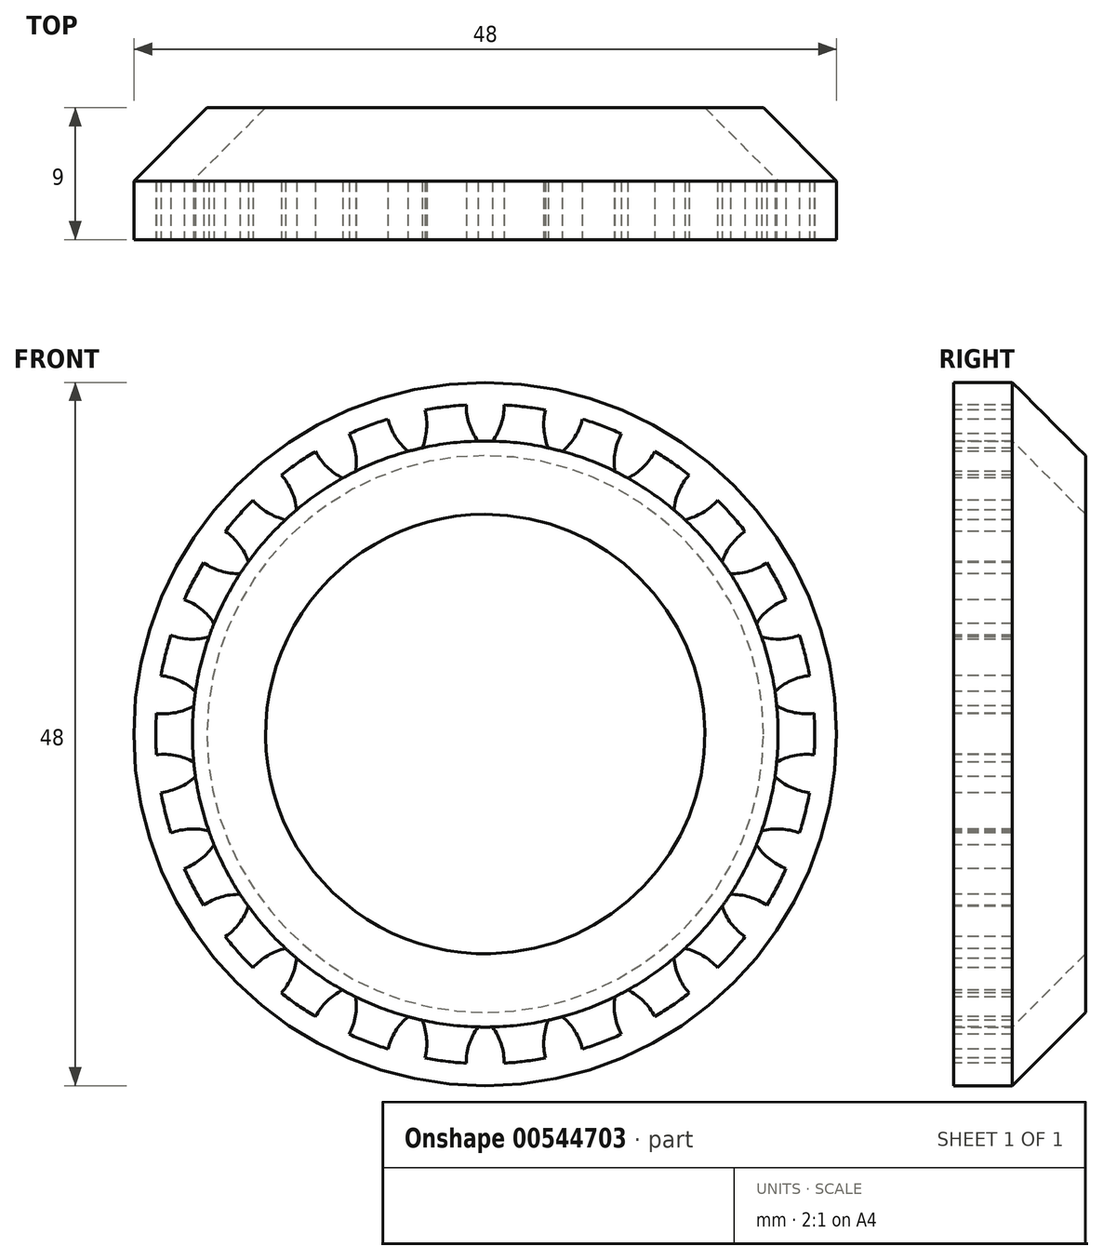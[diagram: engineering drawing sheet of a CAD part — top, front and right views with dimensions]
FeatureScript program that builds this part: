
annotation { "Feature Type Name" : "Feature", "Feature Type Description" : "" }
export const myFeature = defineFeature(function(context is Context, id is Id, definition is map)
    precondition{}
    {
        {
            var Q0;
            Q0=qCreatedBy(makeId("Right.planeOp"),FACE);
            var sketch = newSketch(context, id + "F0", { "sketchPlane" : qUnion([Q0])});
            skLineSegment(sketch, "E0", {"start": v(0, 0) * mm, "end": v(-8.99, 0) * mm, "construction": true});
            skLineSegment(sketch, "E1", {"start": v(0, 20) * mm, "end": v(4, 20) * mm});
            skLineSegment(sketch, "E2", {"start": v(4, 20) * mm, "end": v(9, 15) * mm});
            skLineSegment(sketch, "E3", {"start": v(9, 15) * mm, "end": v(9, 19) * mm});
            skLineSegment(sketch, "E4", {"start": v(9, 19) * mm, "end": v(4, 24) * mm});
            skLineSegment(sketch, "E5", {"start": v(4, 24) * mm, "end": v(0, 24) * mm});
            skLineSegment(sketch, "E6", {"start": v(0, 24) * mm, "end": v(0, 20) * mm});
            skSolve(sketch);
        }
        {
            var Q0;
            Q0 = qSketchRegion(id + "F0", true);
            var Q1;
            Q1=sQuery(id+"F0.wireOp",EDGE,"E0");
            revolve(context, id + "F1", {"entities" : qUnion([Q0]), "axis" : qUnion([Q1]), "revolveType" : RevolveType.FULL});
        }
        {
            var Q0;
            Q0=qCreatedBy(makeId("Front.planeOp"),FACE);
            var sketch = newSketch(context, id + "F2", { "sketchPlane" : qUnion([Q0])});
            skCircle(sketch, "E7", {"center": v(0, 0) * mm, "radius": 20 * mm});
            skCircle(sketch, "E8", {"center": v(0, 0) * mm, "radius": 24 * mm, "construction": true});
            skCircle(sketch, "E9", {"center": v(0, 0) * mm, "radius": 22.5 * mm});
            skPoint(sketch, "E10", {"position": v(0, 20) * mm});
            skPoint(sketch, "E11", {"position": v(-0.5, 20) * mm});
            skPoint(sketch, "E12", {"position": v(0.5, 20) * mm});
            skPoint(sketch, "E13", {"position": v(0, 22.5) * mm});
            skPoint(sketch, "E14", {"position": v(-1.3, 22.46) * mm});
            skPoint(sketch, "E15", {"position": v(1.3, 22.46) * mm});
            skArc(sketch, "E16", {"start": v(-1.3, 22.46) * mm, "mid": v(-1.1, 21.17) * mm, "end": v(-0.5, 20) * mm});
            skArc(sketch, "E17", {"start": v(0.5, 20) * mm, "mid": v(1.1, 21.17) * mm, "end": v(1.3, 22.46) * mm});
            skLineSegment(sketch, "E18", {"start": v(-0.5, 20) * mm, "end": v(0.5, 20) * mm});
            skPoint(sketch, "E19.1.0", {"position": v(-5.27, 19.3) * mm});
            skArc(sketch, "E19.1.1", {"start": v(-4.3, 19.53) * mm, "mid": v(-4, 20.81) * mm, "end": v(-4.11, 22.12) * mm});
            skArc(sketch, "E19.1.2", {"start": v(-6.64, 21.5) * mm, "mid": v(-6.13, 20.29) * mm, "end": v(-5.27, 19.3) * mm});
            skPoint(sketch, "E19.1.3", {"position": v(-6.64, 21.5) * mm});
            skPoint(sketch, "E19.1.4", {"position": v(-5.38, 21.85) * mm});
            skPoint(sketch, "E19.1.5", {"position": v(-4.3, 19.53) * mm});
            skPoint(sketch, "E19.1.6", {"position": v(-4.11, 22.12) * mm});
            skPoint(sketch, "E19.1.7", {"position": v(-4.79, 19.42) * mm});
            skLineSegment(sketch, "E19.1.8", {"start": v(-5.27, 19.3) * mm, "end": v(-4.3, 19.53) * mm});
            skPoint(sketch, "E19.2.0", {"position": v(-9.73, 17.47) * mm});
            skArc(sketch, "E19.2.1", {"start": v(-8.85, 17.94) * mm, "mid": v(-8.87, 19.25) * mm, "end": v(-9.29, 20.5) * mm});
            skArc(sketch, "E19.2.2", {"start": v(-11.59, 19.29) * mm, "mid": v(-10.8, 18.23) * mm, "end": v(-9.73, 17.47) * mm});
            skPoint(sketch, "E19.2.3", {"position": v(-11.59, 19.29) * mm});
            skPoint(sketch, "E19.2.4", {"position": v(-10.46, 19.92) * mm});
            skPoint(sketch, "E19.2.5", {"position": v(-8.85, 17.94) * mm});
            skPoint(sketch, "E19.2.6", {"position": v(-9.29, 20.5) * mm});
            skPoint(sketch, "E19.2.7", {"position": v(-9.3, 17.7) * mm});
            skLineSegment(sketch, "E19.2.8", {"start": v(-9.73, 17.47) * mm, "end": v(-8.85, 17.94) * mm});
            skPoint(sketch, "E19.3.0", {"position": v(-13.63, 14.63) * mm});
            skArc(sketch, "E19.3.1", {"start": v(-12.88, 15.3) * mm, "mid": v(-13.22, 16.57) * mm, "end": v(-13.92, 17.67) * mm});
            skArc(sketch, "E19.3.2", {"start": v(-15.87, 15.95) * mm, "mid": v(-14.85, 15.12) * mm, "end": v(-13.63, 14.63) * mm});
            skPoint(sketch, "E19.3.3", {"position": v(-15.87, 15.95) * mm});
            skPoint(sketch, "E19.3.4", {"position": v(-14.92, 16.84) * mm});
            skPoint(sketch, "E19.3.5", {"position": v(-12.88, 15.3) * mm});
            skPoint(sketch, "E19.3.6", {"position": v(-13.92, 17.67) * mm});
            skPoint(sketch, "E19.3.7", {"position": v(-13.26, 14.97) * mm});
            skLineSegment(sketch, "E19.3.8", {"start": v(-13.63, 14.63) * mm, "end": v(-12.88, 15.3) * mm});
            skPoint(sketch, "E19.4.0", {"position": v(-16.74, 10.95) * mm});
            skArc(sketch, "E19.4.1", {"start": v(-16.17, 11.77) * mm, "mid": v(-16.8, 12.92) * mm, "end": v(-17.75, 13.83) * mm});
            skArc(sketch, "E19.4.2", {"start": v(-19.22, 11.7) * mm, "mid": v(-18.04, 11.12) * mm, "end": v(-16.74, 10.95) * mm});
            skPoint(sketch, "E19.4.3", {"position": v(-19.22, 11.7) * mm});
            skPoint(sketch, "E19.4.4", {"position": v(-18.52, 12.78) * mm});
            skPoint(sketch, "E19.4.5", {"position": v(-16.17, 11.77) * mm});
            skPoint(sketch, "E19.4.6", {"position": v(-17.75, 13.83) * mm});
            skPoint(sketch, "E19.4.7", {"position": v(-16.46, 11.36) * mm});
            skLineSegment(sketch, "E19.4.8", {"start": v(-16.74, 10.95) * mm, "end": v(-16.17, 11.77) * mm});
            skPoint(sketch, "E19.5.0", {"position": v(-18.87, 6.62) * mm});
            skArc(sketch, "E19.5.1", {"start": v(-18.52, 7.56) * mm, "mid": v(-19.4, 8.53) * mm, "end": v(-20.54, 9.18) * mm});
            skArc(sketch, "E19.5.2", {"start": v(-21.46, 6.75) * mm, "mid": v(-20.18, 6.48) * mm, "end": v(-18.87, 6.62) * mm});
            skPoint(sketch, "E19.5.3", {"position": v(-21.46, 6.75) * mm});
            skPoint(sketch, "E19.5.4", {"position": v(-21.04, 7.98) * mm});
            skPoint(sketch, "E19.5.5", {"position": v(-18.52, 7.56) * mm});
            skPoint(sketch, "E19.5.6", {"position": v(-20.54, 9.18) * mm});
            skPoint(sketch, "E19.5.7", {"position": v(-18.7, 7.1) * mm});
            skLineSegment(sketch, "E19.5.8", {"start": v(-18.87, 6.62) * mm, "end": v(-18.52, 7.56) * mm});
            skPoint(sketch, "E19.6.0", {"position": v(-19.9, 1.91) * mm});
            skArc(sketch, "E19.6.1", {"start": v(-19.79, 2.9) * mm, "mid": v(-20.88, 3.64) * mm, "end": v(-22.14, 4) * mm});
            skArc(sketch, "E19.6.2", {"start": v(-22.46, 1.42) * mm, "mid": v(-21.14, 1.46) * mm, "end": v(-19.9, 1.91) * mm});
            skPoint(sketch, "E19.6.3", {"position": v(-22.46, 1.42) * mm});
            skPoint(sketch, "E19.6.4", {"position": v(-22.34, 2.71) * mm});
            skPoint(sketch, "E19.6.5", {"position": v(-19.79, 2.9) * mm});
            skPoint(sketch, "E19.6.6", {"position": v(-22.14, 4) * mm});
            skPoint(sketch, "E19.6.7", {"position": v(-19.85, 2.41) * mm});
            skLineSegment(sketch, "E19.6.8", {"start": v(-19.9, 1.91) * mm, "end": v(-19.79, 2.9) * mm});
            skPoint(sketch, "E19.7.0", {"position": v(-19.79, -2.9) * mm});
            skArc(sketch, "E19.7.1", {"start": v(-19.9, -1.91) * mm, "mid": v(-21.14, -1.46) * mm, "end": v(-22.46, -1.42) * mm});
            skArc(sketch, "E19.7.2", {"start": v(-22.14, -4) * mm, "mid": v(-20.88, -3.64) * mm, "end": v(-19.79, -2.9) * mm});
            skPoint(sketch, "E19.7.3", {"position": v(-22.14, -4) * mm});
            skPoint(sketch, "E19.7.4", {"position": v(-22.34, -2.71) * mm});
            skPoint(sketch, "E19.7.5", {"position": v(-19.9, -1.91) * mm});
            skPoint(sketch, "E19.7.6", {"position": v(-22.46, -1.42) * mm});
            skPoint(sketch, "E19.7.7", {"position": v(-19.85, -2.41) * mm});
            skLineSegment(sketch, "E19.7.8", {"start": v(-19.79, -2.9) * mm, "end": v(-19.9, -1.91) * mm});
            skPoint(sketch, "E19.8.0", {"position": v(-18.52, -7.56) * mm});
            skArc(sketch, "E19.8.1", {"start": v(-18.87, -6.62) * mm, "mid": v(-20.18, -6.48) * mm, "end": v(-21.46, -6.75) * mm});
            skArc(sketch, "E19.8.2", {"start": v(-20.54, -9.18) * mm, "mid": v(-19.4, -8.53) * mm, "end": v(-18.52, -7.56) * mm});
            skPoint(sketch, "E19.8.3", {"position": v(-20.54, -9.18) * mm});
            skPoint(sketch, "E19.8.4", {"position": v(-21.04, -7.98) * mm});
            skPoint(sketch, "E19.8.5", {"position": v(-18.87, -6.62) * mm});
            skPoint(sketch, "E19.8.6", {"position": v(-21.46, -6.75) * mm});
            skPoint(sketch, "E19.8.7", {"position": v(-18.7, -7.1) * mm});
            skLineSegment(sketch, "E19.8.8", {"start": v(-18.52, -7.56) * mm, "end": v(-18.87, -6.62) * mm});
            skPoint(sketch, "E19.9.0", {"position": v(-16.17, -11.77) * mm});
            skArc(sketch, "E19.9.1", {"start": v(-16.74, -10.95) * mm, "mid": v(-18.04, -11.12) * mm, "end": v(-19.22, -11.7) * mm});
            skArc(sketch, "E19.9.2", {"start": v(-17.75, -13.83) * mm, "mid": v(-16.8, -12.92) * mm, "end": v(-16.17, -11.77) * mm});
            skPoint(sketch, "E19.9.3", {"position": v(-17.75, -13.83) * mm});
            skPoint(sketch, "E19.9.4", {"position": v(-18.52, -12.78) * mm});
            skPoint(sketch, "E19.9.5", {"position": v(-16.74, -10.95) * mm});
            skPoint(sketch, "E19.9.6", {"position": v(-19.22, -11.7) * mm});
            skPoint(sketch, "E19.9.7", {"position": v(-16.46, -11.36) * mm});
            skLineSegment(sketch, "E19.9.8", {"start": v(-16.17, -11.77) * mm, "end": v(-16.74, -10.95) * mm});
            skPoint(sketch, "E19.10.0", {"position": v(-12.88, -15.3) * mm});
            skArc(sketch, "E19.10.1", {"start": v(-13.63, -14.63) * mm, "mid": v(-14.85, -15.12) * mm, "end": v(-15.87, -15.95) * mm});
            skArc(sketch, "E19.10.2", {"start": v(-13.92, -17.67) * mm, "mid": v(-13.22, -16.57) * mm, "end": v(-12.88, -15.3) * mm});
            skPoint(sketch, "E19.10.3", {"position": v(-13.92, -17.67) * mm});
            skPoint(sketch, "E19.10.4", {"position": v(-14.92, -16.84) * mm});
            skPoint(sketch, "E19.10.5", {"position": v(-13.63, -14.63) * mm});
            skPoint(sketch, "E19.10.6", {"position": v(-15.87, -15.95) * mm});
            skPoint(sketch, "E19.10.7", {"position": v(-13.26, -14.97) * mm});
            skLineSegment(sketch, "E19.10.8", {"start": v(-12.88, -15.3) * mm, "end": v(-13.63, -14.63) * mm});
            skPoint(sketch, "E19.11.0", {"position": v(-8.85, -17.94) * mm});
            skArc(sketch, "E19.11.1", {"start": v(-9.73, -17.47) * mm, "mid": v(-10.8, -18.23) * mm, "end": v(-11.59, -19.29) * mm});
            skArc(sketch, "E19.11.2", {"start": v(-9.29, -20.5) * mm, "mid": v(-8.87, -19.25) * mm, "end": v(-8.85, -17.94) * mm});
            skPoint(sketch, "E19.11.3", {"position": v(-9.29, -20.5) * mm});
            skPoint(sketch, "E19.11.4", {"position": v(-10.46, -19.92) * mm});
            skPoint(sketch, "E19.11.5", {"position": v(-9.73, -17.47) * mm});
            skPoint(sketch, "E19.11.6", {"position": v(-11.59, -19.29) * mm});
            skPoint(sketch, "E19.11.7", {"position": v(-9.3, -17.7) * mm});
            skLineSegment(sketch, "E19.11.8", {"start": v(-8.85, -17.94) * mm, "end": v(-9.73, -17.47) * mm});
            skPoint(sketch, "E19.12.0", {"position": v(-4.3, -19.53) * mm});
            skArc(sketch, "E19.12.1", {"start": v(-5.27, -19.3) * mm, "mid": v(-6.13, -20.29) * mm, "end": v(-6.64, -21.5) * mm});
            skArc(sketch, "E19.12.2", {"start": v(-4.11, -22.12) * mm, "mid": v(-4, -20.81) * mm, "end": v(-4.3, -19.53) * mm});
            skPoint(sketch, "E19.12.3", {"position": v(-4.11, -22.12) * mm});
            skPoint(sketch, "E19.12.4", {"position": v(-5.38, -21.85) * mm});
            skPoint(sketch, "E19.12.5", {"position": v(-5.27, -19.3) * mm});
            skPoint(sketch, "E19.12.6", {"position": v(-6.64, -21.5) * mm});
            skPoint(sketch, "E19.12.7", {"position": v(-4.79, -19.42) * mm});
            skLineSegment(sketch, "E19.12.8", {"start": v(-4.3, -19.53) * mm, "end": v(-5.27, -19.3) * mm});
            skPoint(sketch, "E19.13.0", {"position": v(0.5, -20) * mm});
            skArc(sketch, "E19.13.1", {"start": v(-0.5, -20) * mm, "mid": v(-1.1, -21.17) * mm, "end": v(-1.3, -22.46) * mm});
            skArc(sketch, "E19.13.2", {"start": v(1.3, -22.46) * mm, "mid": v(1.1, -21.17) * mm, "end": v(0.5, -20) * mm});
            skPoint(sketch, "E19.13.3", {"position": v(1.3, -22.46) * mm});
            skPoint(sketch, "E19.13.4", {"position": v(0, -22.5) * mm});
            skPoint(sketch, "E19.13.5", {"position": v(-0.5, -20) * mm});
            skPoint(sketch, "E19.13.6", {"position": v(-1.3, -22.46) * mm});
            skPoint(sketch, "E19.13.7", {"position": v(0, -20) * mm});
            skLineSegment(sketch, "E19.13.8", {"start": v(0.5, -20) * mm, "end": v(-0.5, -20) * mm});
            skPoint(sketch, "E19.14.0", {"position": v(5.27, -19.3) * mm});
            skArc(sketch, "E19.14.1", {"start": v(4.3, -19.53) * mm, "mid": v(4, -20.81) * mm, "end": v(4.11, -22.12) * mm});
            skArc(sketch, "E19.14.2", {"start": v(6.64, -21.5) * mm, "mid": v(6.13, -20.29) * mm, "end": v(5.27, -19.3) * mm});
            skPoint(sketch, "E19.14.3", {"position": v(6.64, -21.5) * mm});
            skPoint(sketch, "E19.14.4", {"position": v(5.38, -21.85) * mm});
            skPoint(sketch, "E19.14.5", {"position": v(4.3, -19.53) * mm});
            skPoint(sketch, "E19.14.6", {"position": v(4.11, -22.12) * mm});
            skPoint(sketch, "E19.14.7", {"position": v(4.79, -19.42) * mm});
            skLineSegment(sketch, "E19.14.8", {"start": v(5.27, -19.3) * mm, "end": v(4.3, -19.53) * mm});
            skPoint(sketch, "E19.15.0", {"position": v(9.73, -17.47) * mm});
            skArc(sketch, "E19.15.1", {"start": v(8.85, -17.94) * mm, "mid": v(8.87, -19.25) * mm, "end": v(9.29, -20.5) * mm});
            skArc(sketch, "E19.15.2", {"start": v(11.59, -19.29) * mm, "mid": v(10.8, -18.23) * mm, "end": v(9.73, -17.47) * mm});
            skPoint(sketch, "E19.15.3", {"position": v(11.59, -19.29) * mm});
            skPoint(sketch, "E19.15.4", {"position": v(10.46, -19.92) * mm});
            skPoint(sketch, "E19.15.5", {"position": v(8.85, -17.94) * mm});
            skPoint(sketch, "E19.15.6", {"position": v(9.29, -20.5) * mm});
            skPoint(sketch, "E19.15.7", {"position": v(9.3, -17.7) * mm});
            skLineSegment(sketch, "E19.15.8", {"start": v(9.73, -17.47) * mm, "end": v(8.85, -17.94) * mm});
            skPoint(sketch, "E19.16.0", {"position": v(13.63, -14.63) * mm});
            skArc(sketch, "E19.16.1", {"start": v(12.88, -15.3) * mm, "mid": v(13.22, -16.57) * mm, "end": v(13.92, -17.67) * mm});
            skArc(sketch, "E19.16.2", {"start": v(15.87, -15.95) * mm, "mid": v(14.85, -15.12) * mm, "end": v(13.63, -14.63) * mm});
            skPoint(sketch, "E19.16.3", {"position": v(15.87, -15.95) * mm});
            skPoint(sketch, "E19.16.4", {"position": v(14.92, -16.84) * mm});
            skPoint(sketch, "E19.16.5", {"position": v(12.88, -15.3) * mm});
            skPoint(sketch, "E19.16.6", {"position": v(13.92, -17.67) * mm});
            skPoint(sketch, "E19.16.7", {"position": v(13.26, -14.97) * mm});
            skLineSegment(sketch, "E19.16.8", {"start": v(13.63, -14.63) * mm, "end": v(12.88, -15.3) * mm});
            skPoint(sketch, "E19.17.0", {"position": v(16.74, -10.95) * mm});
            skArc(sketch, "E19.17.1", {"start": v(16.17, -11.77) * mm, "mid": v(16.8, -12.92) * mm, "end": v(17.75, -13.83) * mm});
            skArc(sketch, "E19.17.2", {"start": v(19.22, -11.7) * mm, "mid": v(18.04, -11.12) * mm, "end": v(16.74, -10.95) * mm});
            skPoint(sketch, "E19.17.3", {"position": v(19.22, -11.7) * mm});
            skPoint(sketch, "E19.17.4", {"position": v(18.52, -12.78) * mm});
            skPoint(sketch, "E19.17.5", {"position": v(16.17, -11.77) * mm});
            skPoint(sketch, "E19.17.6", {"position": v(17.75, -13.83) * mm});
            skPoint(sketch, "E19.17.7", {"position": v(16.46, -11.36) * mm});
            skLineSegment(sketch, "E19.17.8", {"start": v(16.74, -10.95) * mm, "end": v(16.17, -11.77) * mm});
            skPoint(sketch, "E19.18.0", {"position": v(18.87, -6.62) * mm});
            skArc(sketch, "E19.18.1", {"start": v(18.52, -7.56) * mm, "mid": v(19.4, -8.53) * mm, "end": v(20.54, -9.18) * mm});
            skArc(sketch, "E19.18.2", {"start": v(21.46, -6.75) * mm, "mid": v(20.18, -6.48) * mm, "end": v(18.87, -6.62) * mm});
            skPoint(sketch, "E19.18.3", {"position": v(21.46, -6.75) * mm});
            skPoint(sketch, "E19.18.4", {"position": v(21.04, -7.98) * mm});
            skPoint(sketch, "E19.18.5", {"position": v(18.52, -7.56) * mm});
            skPoint(sketch, "E19.18.6", {"position": v(20.54, -9.18) * mm});
            skPoint(sketch, "E19.18.7", {"position": v(18.7, -7.1) * mm});
            skLineSegment(sketch, "E19.18.8", {"start": v(18.87, -6.62) * mm, "end": v(18.52, -7.56) * mm});
            skPoint(sketch, "E19.19.0", {"position": v(19.9, -1.91) * mm});
            skArc(sketch, "E19.19.1", {"start": v(19.79, -2.9) * mm, "mid": v(20.88, -3.64) * mm, "end": v(22.14, -4) * mm});
            skArc(sketch, "E19.19.2", {"start": v(22.46, -1.42) * mm, "mid": v(21.14, -1.46) * mm, "end": v(19.9, -1.91) * mm});
            skPoint(sketch, "E19.19.3", {"position": v(22.46, -1.42) * mm});
            skPoint(sketch, "E19.19.4", {"position": v(22.34, -2.71) * mm});
            skPoint(sketch, "E19.19.5", {"position": v(19.79, -2.9) * mm});
            skPoint(sketch, "E19.19.6", {"position": v(22.14, -4) * mm});
            skPoint(sketch, "E19.19.7", {"position": v(19.85, -2.41) * mm});
            skLineSegment(sketch, "E19.19.8", {"start": v(19.9, -1.91) * mm, "end": v(19.79, -2.9) * mm});
            skPoint(sketch, "E19.20.0", {"position": v(19.79, 2.9) * mm});
            skArc(sketch, "E19.20.1", {"start": v(19.9, 1.91) * mm, "mid": v(21.14, 1.46) * mm, "end": v(22.46, 1.42) * mm});
            skArc(sketch, "E19.20.2", {"start": v(22.14, 4) * mm, "mid": v(20.88, 3.64) * mm, "end": v(19.79, 2.9) * mm});
            skPoint(sketch, "E19.20.3", {"position": v(22.14, 4) * mm});
            skPoint(sketch, "E19.20.4", {"position": v(22.34, 2.71) * mm});
            skPoint(sketch, "E19.20.5", {"position": v(19.9, 1.91) * mm});
            skPoint(sketch, "E19.20.6", {"position": v(22.46, 1.42) * mm});
            skPoint(sketch, "E19.20.7", {"position": v(19.85, 2.41) * mm});
            skLineSegment(sketch, "E19.20.8", {"start": v(19.79, 2.9) * mm, "end": v(19.9, 1.91) * mm});
            skPoint(sketch, "E19.21.0", {"position": v(18.52, 7.56) * mm});
            skArc(sketch, "E19.21.1", {"start": v(18.87, 6.62) * mm, "mid": v(20.18, 6.48) * mm, "end": v(21.46, 6.75) * mm});
            skArc(sketch, "E19.21.2", {"start": v(20.54, 9.18) * mm, "mid": v(19.4, 8.53) * mm, "end": v(18.52, 7.56) * mm});
            skPoint(sketch, "E19.21.3", {"position": v(20.54, 9.18) * mm});
            skPoint(sketch, "E19.21.4", {"position": v(21.04, 7.98) * mm});
            skPoint(sketch, "E19.21.5", {"position": v(18.87, 6.62) * mm});
            skPoint(sketch, "E19.21.6", {"position": v(21.46, 6.75) * mm});
            skPoint(sketch, "E19.21.7", {"position": v(18.7, 7.1) * mm});
            skLineSegment(sketch, "E19.21.8", {"start": v(18.52, 7.56) * mm, "end": v(18.87, 6.62) * mm});
            skPoint(sketch, "E19.22.0", {"position": v(16.17, 11.77) * mm});
            skArc(sketch, "E19.22.1", {"start": v(16.74, 10.95) * mm, "mid": v(18.04, 11.12) * mm, "end": v(19.22, 11.7) * mm});
            skArc(sketch, "E19.22.2", {"start": v(17.75, 13.83) * mm, "mid": v(16.8, 12.92) * mm, "end": v(16.17, 11.77) * mm});
            skPoint(sketch, "E19.22.3", {"position": v(17.75, 13.83) * mm});
            skPoint(sketch, "E19.22.4", {"position": v(18.52, 12.78) * mm});
            skPoint(sketch, "E19.22.5", {"position": v(16.74, 10.95) * mm});
            skPoint(sketch, "E19.22.6", {"position": v(19.22, 11.7) * mm});
            skPoint(sketch, "E19.22.7", {"position": v(16.46, 11.36) * mm});
            skLineSegment(sketch, "E19.22.8", {"start": v(16.17, 11.77) * mm, "end": v(16.74, 10.95) * mm});
            skPoint(sketch, "E19.23.0", {"position": v(12.88, 15.3) * mm});
            skArc(sketch, "E19.23.1", {"start": v(13.63, 14.63) * mm, "mid": v(14.85, 15.12) * mm, "end": v(15.87, 15.95) * mm});
            skArc(sketch, "E19.23.2", {"start": v(13.92, 17.67) * mm, "mid": v(13.22, 16.57) * mm, "end": v(12.88, 15.3) * mm});
            skPoint(sketch, "E19.23.3", {"position": v(13.92, 17.67) * mm});
            skPoint(sketch, "E19.23.4", {"position": v(14.92, 16.84) * mm});
            skPoint(sketch, "E19.23.5", {"position": v(13.63, 14.63) * mm});
            skPoint(sketch, "E19.23.6", {"position": v(15.87, 15.95) * mm});
            skPoint(sketch, "E19.23.7", {"position": v(13.26, 14.97) * mm});
            skLineSegment(sketch, "E19.23.8", {"start": v(12.88, 15.3) * mm, "end": v(13.63, 14.63) * mm});
            skPoint(sketch, "E19.24.0", {"position": v(8.85, 17.94) * mm});
            skArc(sketch, "E19.24.1", {"start": v(9.73, 17.47) * mm, "mid": v(10.8, 18.23) * mm, "end": v(11.59, 19.29) * mm});
            skArc(sketch, "E19.24.2", {"start": v(9.29, 20.5) * mm, "mid": v(8.87, 19.25) * mm, "end": v(8.85, 17.94) * mm});
            skPoint(sketch, "E19.24.3", {"position": v(9.29, 20.5) * mm});
            skPoint(sketch, "E19.24.4", {"position": v(10.46, 19.92) * mm});
            skPoint(sketch, "E19.24.5", {"position": v(9.73, 17.47) * mm});
            skPoint(sketch, "E19.24.6", {"position": v(11.59, 19.29) * mm});
            skPoint(sketch, "E19.24.7", {"position": v(9.3, 17.7) * mm});
            skLineSegment(sketch, "E19.24.8", {"start": v(8.85, 17.94) * mm, "end": v(9.73, 17.47) * mm});
            skPoint(sketch, "E20.0.25.0", {"position": v(4.3, 19.53) * mm});
            skArc(sketch, "E20.1.25.0", {"start": v(5.27, 19.3) * mm, "mid": v(6.13, 20.29) * mm, "end": v(6.64, 21.5) * mm});
            skArc(sketch, "E20.5.25.0", {"start": v(4.11, 22.12) * mm, "mid": v(4, 20.81) * mm, "end": v(4.3, 19.53) * mm});
            skPoint(sketch, "E20.9.25.0", {"position": v(4.11, 22.12) * mm});
            skPoint(sketch, "E20.10.25.0", {"position": v(5.38, 21.85) * mm});
            skPoint(sketch, "E20.11.25.0", {"position": v(5.27, 19.3) * mm});
            skPoint(sketch, "E20.12.25.0", {"position": v(6.64, 21.5) * mm});
            skPoint(sketch, "E20.13.25.0", {"position": v(4.79, 19.42) * mm});
            skLineSegment(sketch, "E20.14.25.0", {"start": v(4.3, 19.53) * mm, "end": v(5.27, 19.3) * mm});
            skSolve(sketch);
        }
        {
            var Q0;
            {var subQ0=sQuery(id+"F2.wireOp",EDGE,"E16");Q0=makeQuery(id+"F2.imprint","IMPRINT",FACE,{"disambiguationData":[TD([[makeQuery(id+"F2.imprint","IMPRINT",EDGE,{"derivedFrom":subQ0}),-1.0]])]});}
            var Q1;
            {var subQ0=sQuery(id+"F2.wireOp",EDGE,"E17");Q1=makeQuery(id+"F2.imprint","IMPRINT",FACE,{"disambiguationData":[TD([[makeQuery(id+"F2.imprint","IMPRINT",EDGE,{"derivedFrom":subQ0}),-1.0]])]});}
            var Q2;
            {var subQ0=sQuery(id+"F2.wireOp",EDGE,"E19.23.2");Q2=makeQuery(id+"F2.imprint","IMPRINT",FACE,{"disambiguationData":[TD([[makeQuery(id+"F2.imprint","IMPRINT",EDGE,{"derivedFrom":subQ0}),-1.0]])]});}
            var Q3;
            {var subQ0=sQuery(id+"F2.wireOp",EDGE,"E19.22.2");Q3=makeQuery(id+"F2.imprint","IMPRINT",FACE,{"disambiguationData":[TD([[makeQuery(id+"F2.imprint","IMPRINT",EDGE,{"derivedFrom":subQ0}),-1.0]])]});}
            var Q4;
            {var subQ0=sQuery(id+"F2.wireOp",EDGE,"E19.21.2");Q4=makeQuery(id+"F2.imprint","IMPRINT",FACE,{"disambiguationData":[TD([[makeQuery(id+"F2.imprint","IMPRINT",EDGE,{"derivedFrom":subQ0}),-1.0]])]});}
            var Q5;
            {var subQ0=sQuery(id+"F2.wireOp",EDGE,"E19.20.2");Q5=makeQuery(id+"F2.imprint","IMPRINT",FACE,{"disambiguationData":[TD([[makeQuery(id+"F2.imprint","IMPRINT",EDGE,{"derivedFrom":subQ0}),-1.0]])]});}
            var Q6;
            {var subQ0=sQuery(id+"F2.wireOp",EDGE,"E19.19.2");Q6=makeQuery(id+"F2.imprint","IMPRINT",FACE,{"disambiguationData":[TD([[makeQuery(id+"F2.imprint","IMPRINT",EDGE,{"derivedFrom":subQ0}),-1.0]])]});}
            var Q7;
            {var subQ0=sQuery(id+"F2.wireOp",EDGE,"E19.18.2");Q7=makeQuery(id+"F2.imprint","IMPRINT",FACE,{"disambiguationData":[TD([[makeQuery(id+"F2.imprint","IMPRINT",EDGE,{"derivedFrom":subQ0}),-1.0]])]});}
            var Q8;
            {var subQ0=sQuery(id+"F2.wireOp",EDGE,"E19.17.2");Q8=makeQuery(id+"F2.imprint","IMPRINT",FACE,{"disambiguationData":[TD([[makeQuery(id+"F2.imprint","IMPRINT",EDGE,{"derivedFrom":subQ0}),-1.0]])]});}
            var Q9;
            {var subQ0=sQuery(id+"F2.wireOp",EDGE,"E19.16.2");Q9=makeQuery(id+"F2.imprint","IMPRINT",FACE,{"disambiguationData":[TD([[makeQuery(id+"F2.imprint","IMPRINT",EDGE,{"derivedFrom":subQ0}),-1.0]])]});}
            var Q10;
            {var subQ0=sQuery(id+"F2.wireOp",EDGE,"E19.15.2");Q10=makeQuery(id+"F2.imprint","IMPRINT",FACE,{"disambiguationData":[TD([[makeQuery(id+"F2.imprint","IMPRINT",EDGE,{"derivedFrom":subQ0}),-1.0]])]});}
            var Q11;
            {var subQ0=sQuery(id+"F2.wireOp",EDGE,"E19.14.2");Q11=makeQuery(id+"F2.imprint","IMPRINT",FACE,{"disambiguationData":[TD([[makeQuery(id+"F2.imprint","IMPRINT",EDGE,{"derivedFrom":subQ0}),-1.0]])]});}
            var Q12;
            {var subQ0=sQuery(id+"F2.wireOp",EDGE,"E19.13.2");Q12=makeQuery(id+"F2.imprint","IMPRINT",FACE,{"disambiguationData":[TD([[makeQuery(id+"F2.imprint","IMPRINT",EDGE,{"derivedFrom":subQ0}),-1.0]])]});}
            var Q13;
            {var subQ0=sQuery(id+"F2.wireOp",EDGE,"E19.12.2");Q13=makeQuery(id+"F2.imprint","IMPRINT",FACE,{"disambiguationData":[TD([[makeQuery(id+"F2.imprint","IMPRINT",EDGE,{"derivedFrom":subQ0}),-1.0]])]});}
            var Q14;
            {var subQ0=sQuery(id+"F2.wireOp",EDGE,"E19.11.2");Q14=makeQuery(id+"F2.imprint","IMPRINT",FACE,{"disambiguationData":[TD([[makeQuery(id+"F2.imprint","IMPRINT",EDGE,{"derivedFrom":subQ0}),-1.0]])]});}
            var Q15;
            {var subQ0=sQuery(id+"F2.wireOp",EDGE,"E19.10.2");Q15=makeQuery(id+"F2.imprint","IMPRINT",FACE,{"disambiguationData":[TD([[makeQuery(id+"F2.imprint","IMPRINT",EDGE,{"derivedFrom":subQ0}),-1.0]])]});}
            var Q16;
            {var subQ0=sQuery(id+"F2.wireOp",EDGE,"E19.9.2");Q16=makeQuery(id+"F2.imprint","IMPRINT",FACE,{"disambiguationData":[TD([[makeQuery(id+"F2.imprint","IMPRINT",EDGE,{"derivedFrom":subQ0}),-1.0]])]});}
            var Q17;
            {var subQ0=sQuery(id+"F2.wireOp",EDGE,"E19.8.2");Q17=makeQuery(id+"F2.imprint","IMPRINT",FACE,{"disambiguationData":[TD([[makeQuery(id+"F2.imprint","IMPRINT",EDGE,{"derivedFrom":subQ0}),-1.0]])]});}
            var Q18;
            {var subQ0=sQuery(id+"F2.wireOp",EDGE,"E19.7.2");Q18=makeQuery(id+"F2.imprint","IMPRINT",FACE,{"disambiguationData":[TD([[makeQuery(id+"F2.imprint","IMPRINT",EDGE,{"derivedFrom":subQ0}),-1.0]])]});}
            var Q19;
            {var subQ0=sQuery(id+"F2.wireOp",EDGE,"E19.6.2");Q19=makeQuery(id+"F2.imprint","IMPRINT",FACE,{"disambiguationData":[TD([[makeQuery(id+"F2.imprint","IMPRINT",EDGE,{"derivedFrom":subQ0}),-1.0]])]});}
            var Q20;
            {var subQ0=sQuery(id+"F2.wireOp",EDGE,"E19.5.2");Q20=makeQuery(id+"F2.imprint","IMPRINT",FACE,{"disambiguationData":[TD([[makeQuery(id+"F2.imprint","IMPRINT",EDGE,{"derivedFrom":subQ0}),-1.0]])]});}
            var Q21;
            {var subQ0=sQuery(id+"F2.wireOp",EDGE,"E19.4.2");Q21=makeQuery(id+"F2.imprint","IMPRINT",FACE,{"disambiguationData":[TD([[makeQuery(id+"F2.imprint","IMPRINT",EDGE,{"derivedFrom":subQ0}),-1.0]])]});}
            var Q22;
            {var subQ0=sQuery(id+"F2.wireOp",EDGE,"E19.3.2");Q22=makeQuery(id+"F2.imprint","IMPRINT",FACE,{"disambiguationData":[TD([[makeQuery(id+"F2.imprint","IMPRINT",EDGE,{"derivedFrom":subQ0}),-1.0]])]});}
            var Q23;
            {var subQ0=sQuery(id+"F2.wireOp",EDGE,"E19.2.2");Q23=makeQuery(id+"F2.imprint","IMPRINT",FACE,{"disambiguationData":[TD([[makeQuery(id+"F2.imprint","IMPRINT",EDGE,{"derivedFrom":subQ0}),-1.0]])]});}
            var Q24;
            {var subQ0=sQuery(id+"F2.wireOp",EDGE,"E19.1.2");Q24=makeQuery(id+"F2.imprint","IMPRINT",FACE,{"disambiguationData":[TD([[makeQuery(id+"F2.imprint","IMPRINT",EDGE,{"derivedFrom":subQ0}),-1.0]])]});}
            var Q25;
            {var subQ0=sQuery(id+"F2.wireOp",EDGE,"E19.24.2");Q25=makeQuery(id+"F2.imprint","IMPRINT",FACE,{"disambiguationData":[TD([[makeQuery(id+"F2.imprint","IMPRINT",EDGE,{"derivedFrom":subQ0}),-1.0]])]});}
            extrude(context, id + "F3", {"entities" : qUnion([Q0, Q1, Q2, Q3, Q4, Q5, Q6, Q7, Q8, Q9, Q10, Q11, Q12, Q13, Q14, Q15, Q16, Q17, Q18, Q19, Q20, Q21, Q22, Q23, Q24, Q25]), "operationType" : NewBodyOperationType.REMOVE, "oppositeDirection" : true, "depth" : 4 * mm, "offsetDistance" : 25 * mm});
        }
    });
